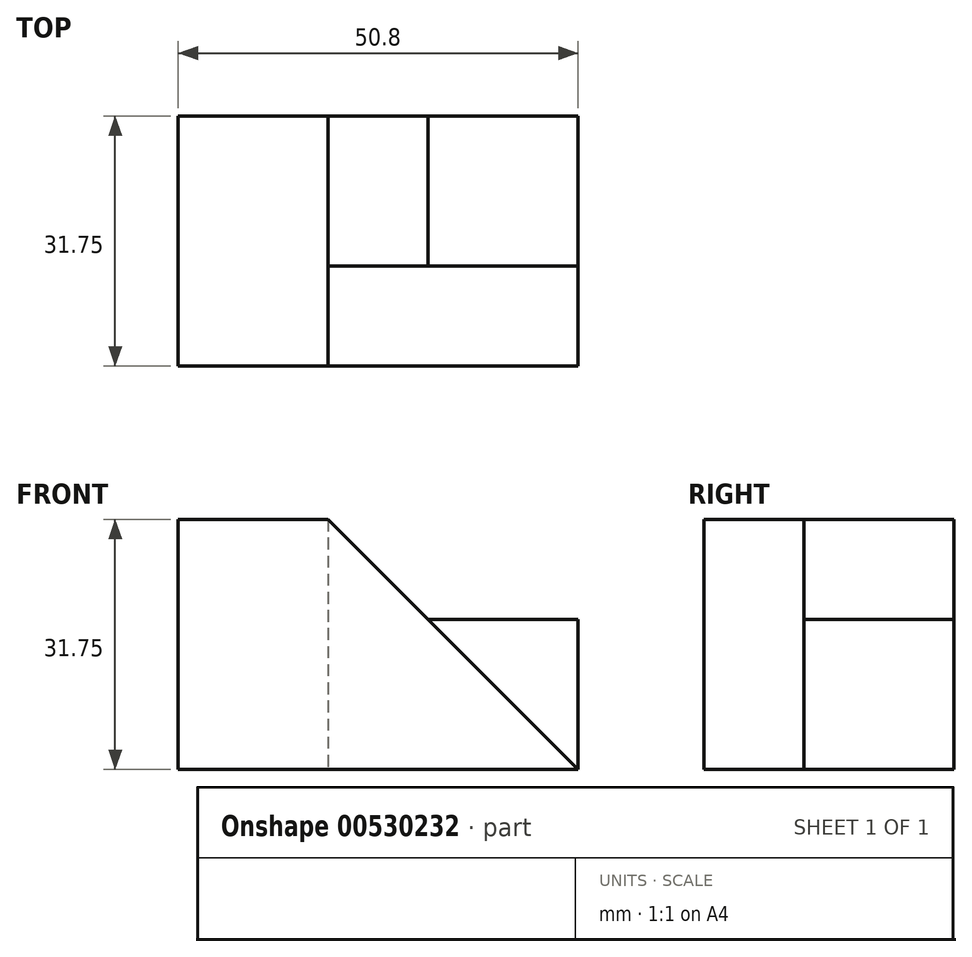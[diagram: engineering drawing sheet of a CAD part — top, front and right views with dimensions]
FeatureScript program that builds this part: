
annotation { "Feature Type Name" : "Feature", "Feature Type Description" : "" }
export const myFeature = defineFeature(function(context is Context, id is Id, definition is map)
    precondition{}
    {
        {
            var Q0;
            Q0=qCreatedBy(makeId("Front.planeOp"),FACE);
            var sketch = newSketch(context, id + "F0", { "sketchPlane" : qUnion([Q0])});
            skLineSegment(sketch, "E0", {"start": v(-62.66, 0) * mm, "end": v(-43.61, 0) * mm});
            skLineSegment(sketch, "E1", {"start": v(-43.61, 0) * mm, "end": v(-43.61, 31.75) * mm});
            skLineSegment(sketch, "E2", {"start": v(-43.61, 31.75) * mm, "end": v(-62.66, 31.75) * mm});
            skLineSegment(sketch, "E3", {"start": v(-62.66, 31.75) * mm, "end": v(-62.66, 0) * mm});
            skSolve(sketch);
        }
        {
            var Q0;
            Q0=makeQuery(id+"F0.imprint","IMPRINT",FACE,{"disambiguationData":[TD([[makeQuery(id+"F0.imprint","IMPRINT",EDGE,{"derivedFrom":sQuery(id+"F0.wireOp",EDGE,"E0")}),1.0]])]});
            extrude(context, id + "F1", {"entities" : qUnion([Q0]), "depth" : 31.75 * mm, "offsetDistance" : 25.4 * mm});
        }
        {
            var Q0;
            Q0=makeQuery(id+"F1.opExtrude","SWEPT_FACE",FACE,{"disambiguationData":[OSD([sQuery(id+"F0.wireOp",EDGE,"E1")])]});
            var sketch = newSketch(context, id + "F2", { "sketchPlane" : qUnion([Q0])});
            skLineSegment(sketch, "E4", {"start": v(-19.05, 31.75) * mm, "end": v(-19.05, 0) * mm});
            skLineSegment(sketch, "E5", {"start": v(-19.05, 0) * mm, "end": v(-31.75, 0) * mm});
            skLineSegment(sketch, "E6", {"start": v(-31.75, 0) * mm, "end": v(-31.75, 31.75) * mm});
            skLineSegment(sketch, "E7", {"start": v(-31.75, 31.75) * mm, "end": v(-19.05, 31.75) * mm});
            skSolve(sketch);
        }
        {
            var Q0;
            Q0 = qSketchRegion(id + "F2", true);
            extrude(context, id + "F3", {"entities" : qUnion([Q0]), "operationType" : NewBodyOperationType.ADD, "depth" : 31.75 * mm, "offsetDistance" : 25.4 * mm});
        }
        {
            var Q0;
            Q0=makeQuery(id+"F3.boolean.opBoolean","MERGE",FACE,{"derivedFrom":[makeQuery(id+"F1.opExtrude","CAP_FACE",FACE,{"disambiguationData":[OSD([sQuery(id+"F0.wireOp",EDGE,"E0"),sQuery(id+"F0.wireOp",EDGE,"E1"),sQuery(id+"F0.wireOp",EDGE,"E2"),sQuery(id+"F0.wireOp",EDGE,"E3")])],"isStart":false}),makeQuery(id+"F3.opExtrude","SWEPT_FACE",FACE,{"disambiguationData":[OSD([sQuery(id+"F2.wireOp",EDGE,"E6")])]})]});
            var sketch = newSketch(context, id + "F4", { "sketchPlane" : qUnion([Q0])});
            skLineSegment(sketch, "E8", {"start": v(-11.86, 0) * mm, "end": v(-43.61, 31.75) * mm});
            skSolve(sketch);
        }
        {
            var Q0;
            {var subQ0=sQuery(id+"F4.wireOp",EDGE,"E8");Q0=makeQuery(id+"F4.imprint","IMPRINT",FACE,{"disambiguationData":[TD([[makeQuery(id+"F4.imprint","IMPRINT",EDGE,{"derivedFrom":subQ0}),-1.0]])]});}
            extrude(context, id + "F5", {"entities" : qUnion([Q0]), "operationType" : NewBodyOperationType.REMOVE, "oppositeDirection" : true, "depth" : 25.4 * mm, "offsetDistance" : 25.4 * mm});
        }
        {
            var Q0;
            Q0=makeQuery(id+"F3.opExtrude","SWEPT_FACE",FACE,{"disambiguationData":[OSD([sQuery(id+"F2.wireOp",EDGE,"E4")])]});
            var sketch = newSketch(context, id + "F6", { "sketchPlane" : qUnion([Q0])});
            skLineSegment(sketch, "E9.bottom", {"start": v(11.86, 0) * mm, "end": v(30.91, 0) * mm});
            skLineSegment(sketch, "E9.top", {"start": v(11.86, 19.05) * mm, "end": v(30.91, 19.05) * mm});
            skLineSegment(sketch, "E9.left", {"start": v(11.86, 0) * mm, "end": v(11.86, 19.05) * mm});
            skLineSegment(sketch, "E9.right", {"start": v(30.91, 0) * mm, "end": v(30.91, 19.05) * mm});
            skSolve(sketch);
        }
        {
            var Q0;
            {var subQ0=sQuery(id+"F6.wireOp",EDGE,"E9.top");Q0=makeQuery(id+"F6.imprint","IMPRINT",FACE,{"disambiguationData":[TD([[makeQuery(id+"F6.imprint","IMPRINT",EDGE,{"derivedFrom":subQ0}),-1.0]])]});}
            extrude(context, id + "F7", {"entities" : qUnion([Q0]), "depth" : 19.05 * mm, "offsetDistance" : 25.4 * mm});
        }
        {
            var Q0;
            Q0=makeQuery(id+"F3.opExtrude","SWEPT_FACE",FACE,{"disambiguationData":[OSD([sQuery(id+"F2.wireOp",EDGE,"E4")])]});
            extrude(context, id + "F8", {"entities" : qUnion([Q0]), "depth" : 19.05 * mm, "offsetDistance" : 25.4 * mm});
        }
    });
